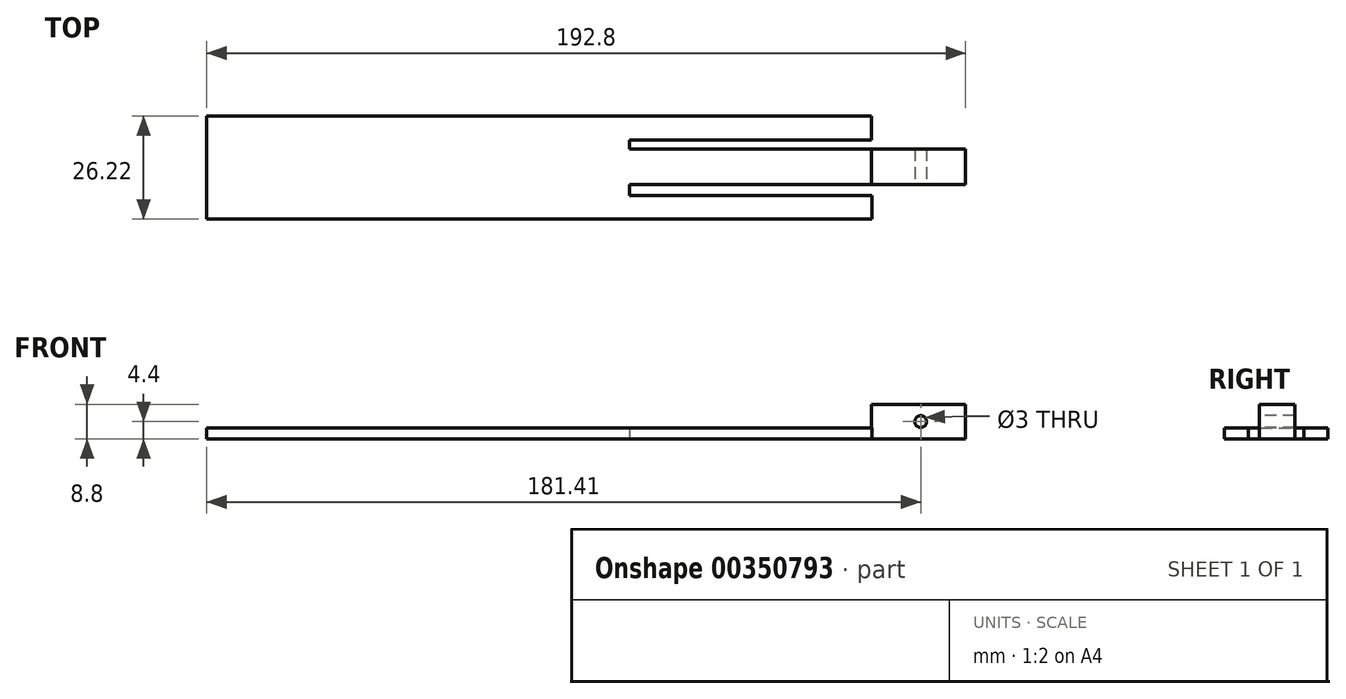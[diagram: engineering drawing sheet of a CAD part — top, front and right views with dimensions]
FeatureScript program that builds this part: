
annotation { "Feature Type Name" : "Feature", "Feature Type Description" : "" }
export const myFeature = defineFeature(function(context is Context, id is Id, definition is map)
    precondition{}
    {
        {
            var Q0;
            Q0=qCreatedBy(makeId("Top.planeOp"),FACE);
            var sketch = newSketch(context, id + "F0", { "sketchPlane" : qUnion([Q0])});
            skLineSegment(sketch, "E0.bottom", {"start": v(75, -12.39) * mm, "end": v(-75, -12.39) * mm});
            skLineSegment(sketch, "E0.top", {"start": v(75, 12.39) * mm, "end": v(-75, 12.39) * mm});
            skLineSegment(sketch, "E0.left", {"start": v(75, -12.39) * mm, "end": v(75, 12.39) * mm});
            skLineSegment(sketch, "E0.right", {"start": v(-75, -12.39) * mm, "end": v(-75, 12.39) * mm});
            skPoint(sketch, "E0.middle", {"position": v(0, 0) * mm});
            skLineSegment(sketch, "E1.bottom", {"start": v(-10.37, 7.78) * mm, "end": v(75, 7.78) * mm});
            skLineSegment(sketch, "E1.top", {"start": v(-10.37, 5.43) * mm, "end": v(75, 5.43) * mm});
            skLineSegment(sketch, "E1.left", {"start": v(-10.37, 7.78) * mm, "end": v(-10.37, 5.43) * mm});
            skLineSegment(sketch, "E2.bottom", {"start": v(-10.37, -3.6) * mm, "end": v(75, -3.6) * mm});
            skLineSegment(sketch, "E2.top", {"start": v(-10.37, -6.34) * mm, "end": v(75, -6.34) * mm});
            skLineSegment(sketch, "E2.left", {"start": v(-10.37, -3.6) * mm, "end": v(-10.37, -6.34) * mm});
            skLineSegment(sketch, "E2.right", {"start": v(75, -3.6) * mm, "end": v(75, -6.34) * mm});
            skSolve(sketch);
        }
        {
            var Q0;
            {var subQ5=sQuery(id+"F0.wireOp",EDGE,"E0.bottom");Q0=makeQuery(id+"F0.imprint","IMPRINT",FACE,{"disambiguationData":[TD([[makeQuery(id+"F0.imprint","IMPRINT",EDGE,{"derivedFrom":subQ5}),-1.0]])]});}
            extrude(context, id + "F1", {"entities" : qUnion([Q0]), "depth" : 2.8 * mm});
        }
        {
            var Q0;
            {var subQ0=sQuery(id+"F0.wireOp",EDGE,"E0.left");Q0=makeQuery(id+"F1.opExtrude","SWEPT_FACE",FACE,{"disambiguationData":[OSD([subQ0]),TDD([makeQuery(id+"F0.imprint","IMPRINT",EDGE,{"disambiguationData":[TD([[makeQuery(id+"F0.imprint","INTERSECT",VERTEX,{"derivedFrom":[sQuery(id+"F0.wireOp",EDGE,"E0.bottom"),subQ0]}),-1.0]])],"derivedFrom":subQ0})])]});}
            extrude(context, id + "F2", {"entities" : qUnion([Q0]), "operationType" : NewBodyOperationType.REMOVE, "oppositeDirection" : true, "depth" : 23.8 * mm});
        }
        {
            var Q0;
            {var subQ0=sQuery(id+"F0.wireOp",EDGE,"E0.left");Q0=makeQuery(id+"F1.opExtrude","SWEPT_FACE",FACE,{"disambiguationData":[OSD([subQ0]),TDD([makeQuery(id+"F0.imprint","IMPRINT",EDGE,{"disambiguationData":[TD([[makeQuery(id+"F0.imprint","INTERSECT",VERTEX,{"derivedFrom":[sQuery(id+"F0.wireOp",EDGE,"E0.top"),subQ0]}),1.0]])],"derivedFrom":subQ0})])]});}
            extrude(context, id + "F3", {"entities" : qUnion([Q0]), "operationType" : NewBodyOperationType.REMOVE, "oppositeDirection" : true, "depth" : 23.9 * mm});
        }
        {
            var Q0;
            Q0=makeQuery(id+"F1.opExtrude","SWEPT_FACE",FACE,{"disambiguationData":[OSD([sQuery(id+"F0.wireOp",EDGE,"E0.right")])]});
            extrude(context, id + "F4", {"entities" : qUnion([Q0]), "operationType" : NewBodyOperationType.ADD, "depth" : 42.8 * mm});
        }
        {
            var Q0;
            {var subQ0=sQuery(id+"F0.wireOp",EDGE,"E0.right");Q0=makeQuery(id+"F4.boolean.opBoolean","MERGE",FACE,{"derivedFrom":[makeQuery(id+"F1.opExtrude","CAP_FACE",FACE,{"disambiguationData":[OSD([sQuery(id+"F0.wireOp",EDGE,"E0.bottom"),sQuery(id+"F0.wireOp",EDGE,"E0.top"),sQuery(id+"F0.wireOp",EDGE,"E0.left"),subQ0,sQuery(id+"F0.wireOp",EDGE,"E1.bottom"),sQuery(id+"F0.wireOp",EDGE,"E1.top"),sQuery(id+"F0.wireOp",EDGE,"E1.left"),sQuery(id+"F0.wireOp",EDGE,"E2.bottom"),sQuery(id+"F0.wireOp",EDGE,"E2.top"),sQuery(id+"F0.wireOp",EDGE,"E2.left")])],"isStart":false}),makeQuery(id+"F4.opExtrude","SWEPT_FACE",FACE,{"disambiguationData":[OSD([subQ0]),TDD([makeQuery(id+"F1.opExtrude","CAP_EDGE",EDGE,{"disambiguationData":[OSD([subQ0])],"isStart":false})])]})]});}
            var sketch = newSketch(context, id + "F5", { "sketchPlane" : qUnion([Q0])});
            skLineSegment(sketch, "E3", {"start": v(51.11, 5.43) * mm, "end": v(51.11, -3.6) * mm});
            skSolve(sketch);
        }
        {
            var Q0;
            {var subQ0=sQuery(id+"F5.wireOp",EDGE,"E3");Q0=makeQuery(id+"F5.imprint","IMPRINT",FACE,{"disambiguationData":[TD([[makeQuery(id+"F5.imprint","IMPRINT",EDGE,{"derivedFrom":subQ0}),1.0]])]});}
            extrude(context, id + "F6", {"entities" : qUnion([Q0]), "operationType" : NewBodyOperationType.ADD, "depth" : 6 * mm});
        }
        {
            var Q0;
            {var subQ0=sQuery(id+"F0.wireOp",EDGE,"E2.bottom");Q0=makeQuery(id+"F6.boolean.opBoolean","MERGE",FACE,{"derivedFrom":[makeQuery(id+"F1.opExtrude","SWEPT_FACE",FACE,{"disambiguationData":[OSD([subQ0])]}),makeQuery(id+"F6.opExtrude","SWEPT_FACE",FACE,{"disambiguationData":[OSD([subQ0])]})]});}
            var sketch = newSketch(context, id + "F7", { "sketchPlane" : qUnion([Q0])});
            skCircle(sketch, "E4", {"center": v(63.6, 4.4) * mm, "radius": 1.5 * mm});
            skPoint(sketch, "E4.centerSnap0", {"position": v(75, 4.4) * mm});
            skSolve(sketch);
        }
        {
            var Q0;
            Q0 = qSketchRegion(id + "F7", true);
            extrude(context, id + "F8", {"entities" : qUnion([Q0]), "operationType" : NewBodyOperationType.REMOVE, "endBound" : BoundingType.UP_TO_NEXT, "oppositeDirection" : true, "depth" : 37 * mm});
        }
        {
            var Q0;
            {var subQ0=sQuery(id+"F0.wireOp",EDGE,"E0.top");Q0=makeQuery(id+"F4.boolean.opBoolean","MERGE",FACE,{"derivedFrom":[makeQuery(id+"F1.opExtrude","SWEPT_FACE",FACE,{"disambiguationData":[OSD([subQ0])]}),makeQuery(id+"F4.opExtrude","SWEPT_FACE",FACE,{"disambiguationData":[OSD([subQ0,sQuery(id+"F0.wireOp",EDGE,"E0.right")])]})]});}
            extrude(context, id + "F9", {"entities" : qUnion([Q0]), "operationType" : NewBodyOperationType.ADD, "depth" : 1.44 * mm});
        }
    });
